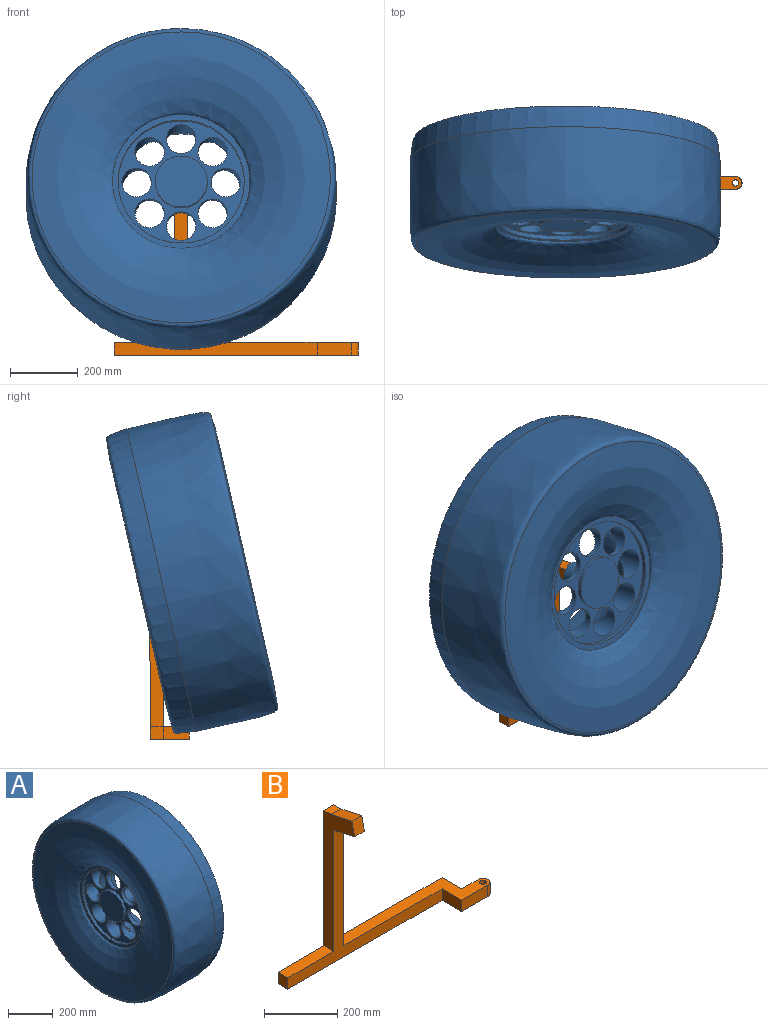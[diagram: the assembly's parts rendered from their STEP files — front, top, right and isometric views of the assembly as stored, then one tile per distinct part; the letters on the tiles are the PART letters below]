
ASSEMBLY  parts=2 mates=1
PART A: 21 faces, bbox 324.6x915.6x915.6 mm
  f0: cylinder r=43.4mm len=93.6mm, axis (-1,0,0), area 11778.5mm2, adj f8,f19
  f1: cylinder r=43.4mm len=93.6mm, axis (-1,0,0), area 11769.1mm2, adj f8,f19
  f2: cylinder r=43.4mm len=93.59mm, axis (-1,0,0), area 11780.6mm2, adj f8,f19
  f3: cylinder r=43.4mm len=93.6mm, axis (-1,0,0), area 11759.2mm2, adj f8,f19
  f4: cylinder r=43.4mm len=93.59mm, axis (-1,0,0), area 11773.3mm2, adj f8,f19
  f5: cylinder r=43.4mm len=93.59mm, axis (-1,0,0), area 11770.4mm2, adj f8,f19
  f6: cylinder r=43.4mm len=93.6mm, axis (-1,0,0), area 11768.8mm2, adj f8,f19
  f7: cylinder r=43.4mm len=93.59mm, axis (-1,0,0), area 11774.3mm2, adj f8,f19
  f8: revolved ~381.06x381.06mm, area 158700.7mm2, adj f0,f1,f2,f3,f4,f5,f6,f7
  f9: plane 406.4x406.4mm, normal (1,0,0), area 15669.6mm2, adj f8,f10
  f10: revolved ~878.84x878.84mm, area 505339.7mm2, adj f9,f11
  f11: revolved ~914.4x914.4mm, area 207382.4mm2, adj f10,f12
  f12: revolved ~915.56x915.56mm, area 738996.1mm2, adj f11,f13
  f13: revolved ~878.84x878.84mm, area 503417.3mm2, adj f12,f14
  f14: plane 406.4x406.4mm, normal (-1,0,0), area 21334.6mm2, adj f13,f18
  f15: plane 76.2x76.2mm, normal (1,0,0), area 4560.4mm2, adj f16
  f16: cylinder r=38.1mm len=76.2mm, axis (-1,0,0), area 18241.5mm2, adj f8,f15
  f17: cylinder r=76.86mm len=153.72mm, axis (-1,0,0), area 6133.3mm2, adj f19,f20
  f18: cylinder r=185.74mm len=371.48mm, axis (-1,0,0), area 14821.4mm2, adj f14,f19
  f19: plane 371.48x371.48mm, normal (-1,0,0), area 42487.5mm2, adj f0,f1,f2,f3,f4,f5,f6,f7
  f20: plane 153.72x153.72mm, normal (-1,0,0), area 18559.6mm2, adj f17
PART B: 18 faces, bbox 717.6x118.7x509.7 mm
  f0: plane 501.65x114.3mm, normal (0,0,1), area 21575.3mm2, adj f1,f2,f3,f4,f5,f6,f7,f9
  f1: plane 596.9x444.5mm, normal (0,-1,0), area 38225.7mm2, adj f0,f2,f8,f10,f11,f12,f13,f15
  f2: plane 76.2x38.1mm, normal (-1,0,0), area 2903.2mm2, adj f0,f1,f3,f11
  f3: plane 101.6x38.1mm, normal (0,-1,0), area 3871mm2, adj f0,f2,f4,f11
  f4: cylinder r=19.05mm len=38.1mm, axis (0,0,-1), area 2280.2mm2, adj f0,f3,f5,f11
  f5: plane 63.5x38.1mm, normal (0,1,0), area 2419.3mm2, adj f0,f4,f6,f11
  f6: plane 76.2x38.1mm, normal (1,0,0), area 2903.2mm2, adj f0,f5,f7,f11
  f7: plane 635x491.68mm, normal (0,1,0), area 41475mm2, adj f0,f6,f8,f10,f11,f12,f13,f14
  f8: plane 38.1x38.1mm, normal (-1,0,0), area 1451.6mm2, adj f1,f7,f10,f11
  f9: cylinder r=9.53mm len=38.1mm, axis (0,0,-1), area 2280.2mm2, adj f0,f11
  f10: plane 177.8x38.1mm, normal (0,0,1), area 6774.2mm2, adj f1,f7,f8,f13
  f11: plane 717.55x114.3mm, normal (0,0,-1), area 29801.1mm2, adj f1,f2,f3,f4,f5,f6,f7,f8
  f12: plane 471.58x118.66mm, normal (1,0,0), area 21023.8mm2, adj f0,f1,f7,f14,f15,f16,f17
  f13: plane 471.58x118.66mm, normal (-1,0,0), area 21023.8mm2, adj f1,f7,f10,f14,f15,f16,f17
  f14: plane 38.1x27.56mm, normal (0,0,1), area 1050mm2, adj f7,f12,f13,f16
  f15: plane 80.56x38.1mm, normal (0,-0.22,-0.98), area 3145.2mm2, adj f1,f12,f13,f17
  f16: plane 80.56x38.1mm, normal (0,0.22,0.98), area 3145.2mm2, adj f12,f13,f14,f17
  f17: plane 47.18x38.1mm, normal (0,-0.98,0.22), area 1842mm2, adj f12,f13,f15,f16
PLACE A rot(axis=(-0.11,0.11,0.99),90.7deg) t=(-370.91,-63.27,403.83)mm
PLACE B rot(axis=(-1,0,0),0.3deg) t=(-288.44,89.37,-83.02)mm
MATE planar A.f16 <-> B.f17  axis (0,0.97,-0.22) through (-370.91,-63.27,403.83)mm
